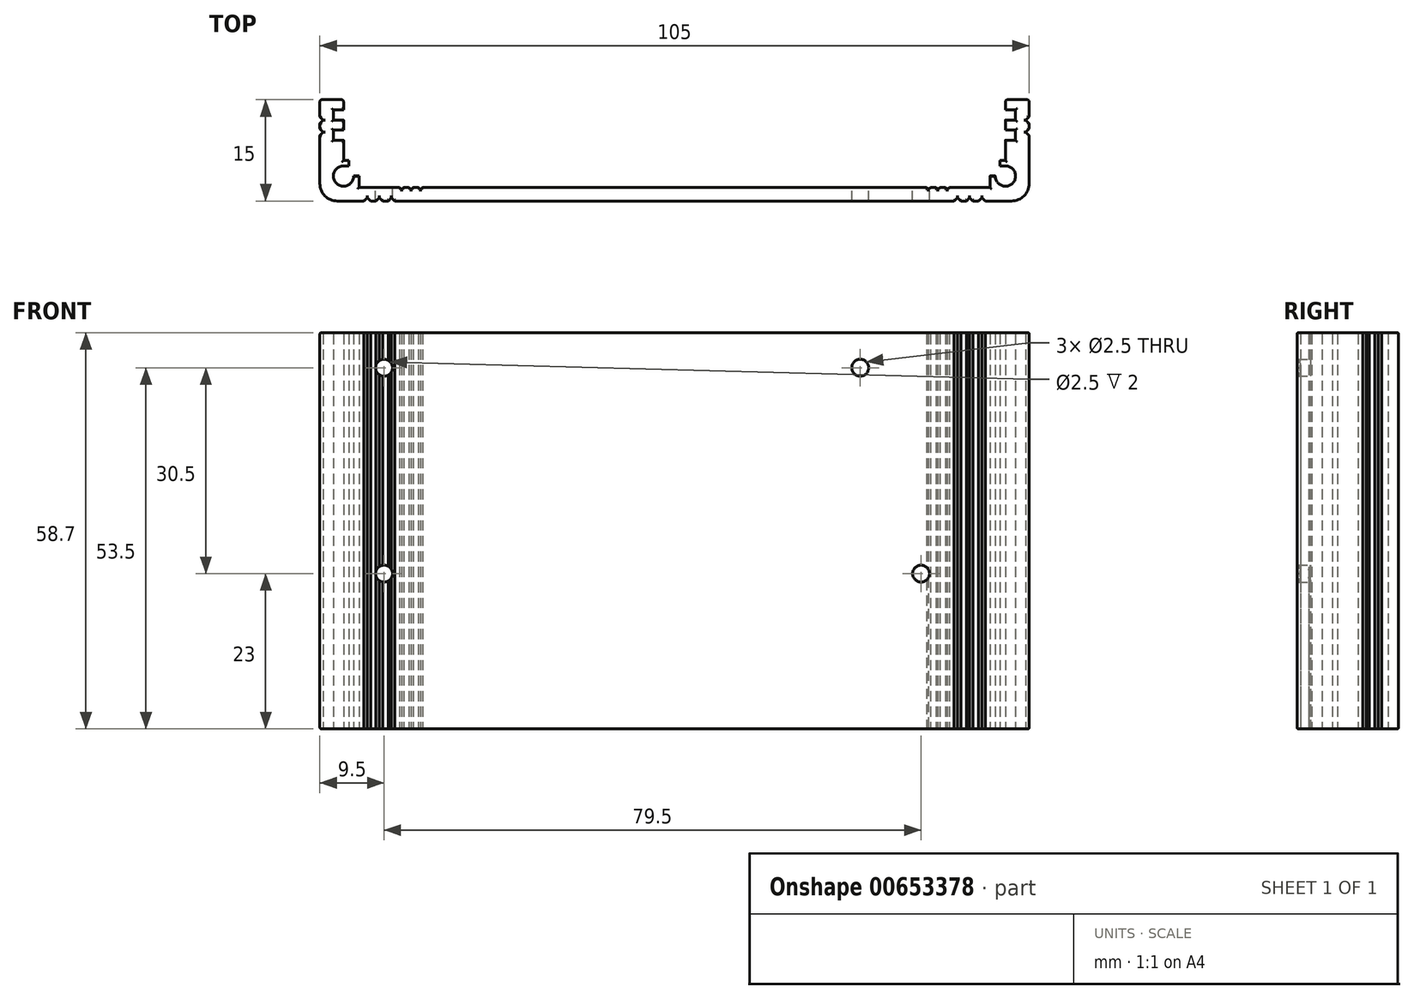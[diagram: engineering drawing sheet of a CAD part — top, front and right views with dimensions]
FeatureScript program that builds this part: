
annotation { "Feature Type Name" : "Feature", "Feature Type Description" : "" }
export const myFeature = defineFeature(function(context is Context, id is Id, definition is map)
    precondition{}
    {
        {
            var Q0;
            Q0=qCreatedBy(makeId("Top.planeOp"),FACE);
            var sketch = newSketch(context, id + "F0", { "sketchPlane" : qUnion([Q0])});
            skLineSegment(sketch, "E0.bottom", {"start": v(52.5, 15) * mm, "end": v(-52.5, 15) * mm, "construction": true});
            skLineSegment(sketch, "E0.top", {"start": v(52.5, -15) * mm, "end": v(-52.5, -15) * mm, "construction": true});
            skLineSegment(sketch, "E0.left", {"start": v(52.5, 15) * mm, "end": v(52.5, -15) * mm, "construction": true});
            skLineSegment(sketch, "E0.right", {"start": v(-52.5, 15) * mm, "end": v(-52.5, -15) * mm, "construction": true});
            skPoint(sketch, "E0.middle", {"position": v(0, 0) * mm});
            skLineSegment(sketch, "E1", {"start": v(-52.5, -15) * mm, "end": v(-46, -15) * mm});
            skLineSegment(sketch, "E2", {"start": v(-46, -15) * mm, "end": v(-45.5, -14.5) * mm});
            skLineSegment(sketch, "E3", {"start": v(-45.5, -14.5) * mm, "end": v(-45, -15) * mm});
            skLineSegment(sketch, "E4", {"start": v(-45, -15) * mm, "end": v(-44.2, -15) * mm});
            skLineSegment(sketch, "E5", {"start": v(-44.2, -15) * mm, "end": v(-43.7, -14.5) * mm});
            skLineSegment(sketch, "E6", {"start": v(-43.7, -14.5) * mm, "end": v(-43.2, -15) * mm});
            skLineSegment(sketch, "E7", {"start": v(-43.2, -15) * mm, "end": v(-42.4, -15) * mm});
            skLineSegment(sketch, "E8", {"start": v(-42.4, -15) * mm, "end": v(-41.9, -14.5) * mm});
            skLineSegment(sketch, "E9", {"start": v(-41.9, -14.5) * mm, "end": v(-41.4, -15) * mm});
            skLineSegment(sketch, "E10", {"start": v(-41.4, -15) * mm, "end": v(0, -15) * mm});
            skLineSegment(sketch, "E11.MirrorCS", {"start": v(52.5, -15) * mm, "end": v(46, -15) * mm});
            skLineSegment(sketch, "E12.MirrorCS", {"start": v(46, -15) * mm, "end": v(45.5, -14.5) * mm});
            skLineSegment(sketch, "E13.MirrorCS", {"start": v(45.5, -14.5) * mm, "end": v(45, -15) * mm});
            skLineSegment(sketch, "E14.MirrorCS", {"start": v(45, -15) * mm, "end": v(44.2, -15) * mm});
            skLineSegment(sketch, "E15.MirrorCS", {"start": v(44.2, -15) * mm, "end": v(43.7, -14.5) * mm});
            skLineSegment(sketch, "E16.MirrorCS", {"start": v(43.7, -14.5) * mm, "end": v(43.2, -15) * mm});
            skLineSegment(sketch, "E17.MirrorCS", {"start": v(43.2, -15) * mm, "end": v(42.4, -15) * mm});
            skLineSegment(sketch, "E18.MirrorCS", {"start": v(42.4, -15) * mm, "end": v(41.9, -14.5) * mm});
            skLineSegment(sketch, "E19.MirrorCS", {"start": v(41.9, -14.5) * mm, "end": v(41.4, -15) * mm});
            skLineSegment(sketch, "E20.MirrorCS", {"start": v(41.4, -15) * mm, "end": v(0, -15) * mm});
            skLineSegment(sketch, "E21", {"start": v(-52.5, 0) * mm, "end": v(-52.5, -2.5) * mm});
            skLineSegment(sketch, "E22", {"start": v(-52.5, -2.5) * mm, "end": v(-52, -3) * mm});
            skLineSegment(sketch, "E23", {"start": v(-52, -3) * mm, "end": v(-52.5, -3.5) * mm});
            skLineSegment(sketch, "E24", {"start": v(-52.5, -3.5) * mm, "end": v(-52.5, -4.3) * mm});
            skLineSegment(sketch, "E25", {"start": v(-52.5, -4.3) * mm, "end": v(-52, -4.8) * mm});
            skLineSegment(sketch, "E26", {"start": v(-52, -4.8) * mm, "end": v(-52.5, -5.3) * mm});
            skLineSegment(sketch, "E27", {"start": v(-52.5, -5.3) * mm, "end": v(-52.5, -15) * mm});
            skLineSegment(sketch, "E28.MirrorCS", {"start": v(52.5, 0) * mm, "end": v(52.5, -2.5) * mm});
            skLineSegment(sketch, "E29.MirrorCS", {"start": v(52.5, -2.5) * mm, "end": v(52, -3) * mm});
            skLineSegment(sketch, "E30.MirrorCS", {"start": v(52, -3) * mm, "end": v(52.5, -3.5) * mm});
            skLineSegment(sketch, "E31.MirrorCS", {"start": v(52.5, -4.3) * mm, "end": v(52, -4.8) * mm});
            skLineSegment(sketch, "E32.MirrorCS", {"start": v(52.5, -3.5) * mm, "end": v(52.5, -4.3) * mm});
            skLineSegment(sketch, "E33.MirrorCS", {"start": v(52, -4.8) * mm, "end": v(52.5, -5.3) * mm});
            skLineSegment(sketch, "E34.MirrorCS", {"start": v(52.5, -5.3) * mm, "end": v(52.5, -15) * mm});
            skLineSegment(sketch, "E35", {"start": v(-52.5, 0) * mm, "end": v(-49, 0) * mm});
            skLineSegment(sketch, "E36", {"start": v(-49, 0) * mm, "end": v(-49, -1.5) * mm});
            skLineSegment(sketch, "E37", {"start": v(-49, -1.5) * mm, "end": v(-50.5, -1.5) * mm});
            skLineSegment(sketch, "E38", {"start": v(-50.5, -1.5) * mm, "end": v(-50.5, -3) * mm});
            skLineSegment(sketch, "E39", {"start": v(-50.5, -3) * mm, "end": v(-49, -3) * mm});
            skLineSegment(sketch, "E40", {"start": v(-49, -3) * mm, "end": v(-49, -4.5) * mm});
            skLineSegment(sketch, "E41", {"start": v(-49, -4.5) * mm, "end": v(-50.5, -4.5) * mm});
            skLineSegment(sketch, "E42", {"start": v(-50.5, -4.5) * mm, "end": v(-50.5, -6) * mm});
            skLineSegment(sketch, "E43", {"start": v(-50.5, -6) * mm, "end": v(-49, -6) * mm});
            skLineSegment(sketch, "E44", {"start": v(-49, -6) * mm, "end": v(-49, -9) * mm});
            skCircle(sketch, "E45", {"center": v(-49, -11.3) * mm, "radius": 1.5 * mm, "construction": true});
            skPoint(sketch, "E45.second.point", {"position": v(-49, -12.8) * mm});
            skPoint(sketch, "E45.third.point", {"position": v(-47.5, -11.3) * mm});
            skLineSegment(sketch, "E46", {"start": v(-49, -12.8) * mm, "end": v(-49, -9.8) * mm, "construction": true});
            skArc(sketch, "E47", {"start": v(-49, -9.8) * mm, "mid": v(-50.06, -12.36) * mm, "end": v(-47.5, -11.3) * mm});
            skLineSegment(sketch, "E48", {"start": v(-47.5, -11.3) * mm, "end": v(-47.5, -11.3) * mm});
            skLineSegment(sketch, "E49", {"start": v(-46.7, -13) * mm, "end": v(-40.7, -13) * mm});
            skLineSegment(sketch, "E50", {"start": v(-40.7, -13) * mm, "end": v(-40.4, -13.3) * mm});
            skLineSegment(sketch, "E51", {"start": v(-40.4, -13.3) * mm, "end": v(-40.1, -13) * mm});
            skLineSegment(sketch, "E52", {"start": v(-40.1, -13) * mm, "end": v(-39.3, -13) * mm});
            skLineSegment(sketch, "E53", {"start": v(-39.3, -13) * mm, "end": v(-39, -13.3) * mm});
            skLineSegment(sketch, "E54", {"start": v(-39, -13.3) * mm, "end": v(-38.7, -13) * mm});
            skLineSegment(sketch, "E55", {"start": v(-38.7, -13) * mm, "end": v(-37.9, -13) * mm});
            skLineSegment(sketch, "E56", {"start": v(-37.9, -13) * mm, "end": v(-37.6, -13.3) * mm});
            skLineSegment(sketch, "E57", {"start": v(-37.6, -13.3) * mm, "end": v(-37.3, -13) * mm});
            skLineSegment(sketch, "E58", {"start": v(-37.3, -13) * mm, "end": v(0, -13) * mm});
            skLineSegment(sketch, "E59", {"start": v(-47.5, -11.3) * mm, "end": v(-46.7, -11.3) * mm});
            skLineSegment(sketch, "E60", {"start": v(-46.7, -11.3) * mm, "end": v(-46.7, -13) * mm});
            skLineSegment(sketch, "E61.MirrorCS", {"start": v(37.3, -13) * mm, "end": v(0, -13) * mm});
            skLineSegment(sketch, "E62.MirrorCS", {"start": v(37.6, -13.3) * mm, "end": v(37.3, -13) * mm});
            skLineSegment(sketch, "E63.MirrorCS", {"start": v(37.9, -13) * mm, "end": v(37.6, -13.3) * mm});
            skLineSegment(sketch, "E64.MirrorCS", {"start": v(39, -13.3) * mm, "end": v(38.7, -13) * mm});
            skLineSegment(sketch, "E65.MirrorCS", {"start": v(39.3, -13) * mm, "end": v(39, -13.3) * mm});
            skLineSegment(sketch, "E66.MirrorCS", {"start": v(40.4, -13.3) * mm, "end": v(40.1, -13) * mm});
            skLineSegment(sketch, "E67.MirrorCS", {"start": v(40.7, -13) * mm, "end": v(40.4, -13.3) * mm});
            skLineSegment(sketch, "E68.MirrorCS", {"start": v(46.7, -13) * mm, "end": v(40.7, -13) * mm});
            skLineSegment(sketch, "E69.MirrorCS", {"start": v(46.7, -11.3) * mm, "end": v(46.7, -13) * mm});
            skLineSegment(sketch, "E70.MirrorCS", {"start": v(49, -6) * mm, "end": v(49, -9) * mm});
            skLineSegment(sketch, "E71.MirrorCS", {"start": v(50.5, -6) * mm, "end": v(49, -6) * mm});
            skLineSegment(sketch, "E72.MirrorCS", {"start": v(50.5, -4.5) * mm, "end": v(50.5, -6) * mm});
            skLineSegment(sketch, "E73.MirrorCS", {"start": v(49, -4.5) * mm, "end": v(50.5, -4.5) * mm});
            skLineSegment(sketch, "E74.MirrorCS", {"start": v(49, -3) * mm, "end": v(49, -4.5) * mm});
            skLineSegment(sketch, "E75.MirrorCS", {"start": v(50.5, -3) * mm, "end": v(49, -3) * mm});
            skLineSegment(sketch, "E76.MirrorCS", {"start": v(50.5, -1.5) * mm, "end": v(50.5, -3) * mm});
            skLineSegment(sketch, "E77.MirrorCS", {"start": v(49, -1.5) * mm, "end": v(50.5, -1.5) * mm});
            skLineSegment(sketch, "E78.MirrorCS", {"start": v(49, 0) * mm, "end": v(49, -1.5) * mm});
            skLineSegment(sketch, "E79.MirrorCS", {"start": v(52.5, 0) * mm, "end": v(49, 0) * mm});
            skLineSegment(sketch, "E80.MirrorCS", {"start": v(38.7, -13) * mm, "end": v(37.9, -13) * mm});
            skLineSegment(sketch, "E81.MirrorCS", {"start": v(40.1, -13) * mm, "end": v(39.3, -13) * mm});
            skLineSegment(sketch, "E82", {"start": v(-49, -9) * mm, "end": v(-48.2, -9) * mm});
            skLineSegment(sketch, "E83", {"start": v(-48.2, -9) * mm, "end": v(-48.2, -9.8) * mm});
            skLineSegment(sketch, "E84", {"start": v(-48.2, -9.8) * mm, "end": v(-49, -9.8) * mm});
            skLineSegment(sketch, "E85", {"start": v(-50.5, -11.3) * mm, "end": v(-47.5, -11.3) * mm, "construction": true});
            skLineSegment(sketch, "E86", {"start": v(-50.5, -11.3) * mm, "end": v(-50.5, -1.5) * mm, "construction": true});
            skArc(sketch, "E87.MirrorCS", {"start": v(49, -9.8) * mm, "mid": v(50.06, -12.36) * mm, "end": v(47.5, -11.3) * mm});
            skLineSegment(sketch, "E88.MirrorCS", {"start": v(49, -9) * mm, "end": v(48.2, -9) * mm});
            skLineSegment(sketch, "E89.MirrorCS", {"start": v(48.2, -9.8) * mm, "end": v(49, -9.8) * mm});
            skLineSegment(sketch, "E90.MirrorCS", {"start": v(48.2, -9) * mm, "end": v(48.2, -9.8) * mm});
            skLineSegment(sketch, "E91.MirrorCS", {"start": v(47.5, -11.3) * mm, "end": v(46.7, -11.3) * mm});
            skSolve(sketch);
        }
        {
            var Q0;
            Q0=makeQuery(id+"F0.imprint","IMPRINT",FACE,{"disambiguationData":[TD([[makeQuery(id+"F0.imprint","IMPRINT",EDGE,{"derivedFrom":sQuery(id+"F0.wireOp",EDGE,"E1")}),1.0]])]});
            extrude(context, id + "F1", {"entities" : qUnion([Q0]), "depth" : 58.7 * mm, "offsetDistance" : 25.4 * mm});
        }
        {
            var Q0;
            Q0=makeQuery(id+"F1.opExtrude","CAP_FACE",FACE,{"disambiguationData":[OSD([sQuery(id+"F0.wireOp",EDGE,"E1"),sQuery(id+"F0.wireOp",EDGE,"E2"),sQuery(id+"F0.wireOp",EDGE,"E3"),sQuery(id+"F0.wireOp",EDGE,"E4"),sQuery(id+"F0.wireOp",EDGE,"E5"),sQuery(id+"F0.wireOp",EDGE,"E6"),sQuery(id+"F0.wireOp",EDGE,"E7"),sQuery(id+"F0.wireOp",EDGE,"E8"),sQuery(id+"F0.wireOp",EDGE,"E9"),sQuery(id+"F0.wireOp",EDGE,"E10"),sQuery(id+"F0.wireOp",EDGE,"E11.MirrorCS"),sQuery(id+"F0.wireOp",EDGE,"E12.MirrorCS"),sQuery(id+"F0.wireOp",EDGE,"E13.MirrorCS"),sQuery(id+"F0.wireOp",EDGE,"E14.MirrorCS"),sQuery(id+"F0.wireOp",EDGE,"E15.MirrorCS"),sQuery(id+"F0.wireOp",EDGE,"E16.MirrorCS"),sQuery(id+"F0.wireOp",EDGE,"E17.MirrorCS"),sQuery(id+"F0.wireOp",EDGE,"E18.MirrorCS"),sQuery(id+"F0.wireOp",EDGE,"E19.MirrorCS"),sQuery(id+"F0.wireOp",EDGE,"E20.MirrorCS"),sQuery(id+"F0.wireOp",EDGE,"E21"),sQuery(id+"F0.wireOp",EDGE,"E22"),sQuery(id+"F0.wireOp",EDGE,"E23"),sQuery(id+"F0.wireOp",EDGE,"E24"),sQuery(id+"F0.wireOp",EDGE,"E25"),sQuery(id+"F0.wireOp",EDGE,"E26"),sQuery(id+"F0.wireOp",EDGE,"E27"),sQuery(id+"F0.wireOp",EDGE,"E28.MirrorCS"),sQuery(id+"F0.wireOp",EDGE,"E29.MirrorCS"),sQuery(id+"F0.wireOp",EDGE,"E30.MirrorCS"),sQuery(id+"F0.wireOp",EDGE,"E31.MirrorCS"),sQuery(id+"F0.wireOp",EDGE,"E32.MirrorCS"),sQuery(id+"F0.wireOp",EDGE,"E33.MirrorCS"),sQuery(id+"F0.wireOp",EDGE,"E34.MirrorCS"),sQuery(id+"F0.wireOp",EDGE,"E35"),sQuery(id+"F0.wireOp",EDGE,"E36"),sQuery(id+"F0.wireOp",EDGE,"E37"),sQuery(id+"F0.wireOp",EDGE,"E38"),sQuery(id+"F0.wireOp",EDGE,"E39"),sQuery(id+"F0.wireOp",EDGE,"E40"),sQuery(id+"F0.wireOp",EDGE,"E41"),sQuery(id+"F0.wireOp",EDGE,"E42"),sQuery(id+"F0.wireOp",EDGE,"E43"),sQuery(id+"F0.wireOp",EDGE,"E44"),sQuery(id+"F0.wireOp",EDGE,"E47"),sQuery(id+"F0.wireOp",EDGE,"E49"),sQuery(id+"F0.wireOp",EDGE,"E50"),sQuery(id+"F0.wireOp",EDGE,"E51"),sQuery(id+"F0.wireOp",EDGE,"E52"),sQuery(id+"F0.wireOp",EDGE,"E53"),sQuery(id+"F0.wireOp",EDGE,"E54"),sQuery(id+"F0.wireOp",EDGE,"E55"),sQuery(id+"F0.wireOp",EDGE,"E56"),sQuery(id+"F0.wireOp",EDGE,"E57"),sQuery(id+"F0.wireOp",EDGE,"E58"),sQuery(id+"F0.wireOp",EDGE,"E59"),sQuery(id+"F0.wireOp",EDGE,"E60"),sQuery(id+"F0.wireOp",EDGE,"E61.MirrorCS"),sQuery(id+"F0.wireOp",EDGE,"E62.MirrorCS"),sQuery(id+"F0.wireOp",EDGE,"E63.MirrorCS"),sQuery(id+"F0.wireOp",EDGE,"E64.MirrorCS"),sQuery(id+"F0.wireOp",EDGE,"E65.MirrorCS"),sQuery(id+"F0.wireOp",EDGE,"E66.MirrorCS"),sQuery(id+"F0.wireOp",EDGE,"E67.MirrorCS"),sQuery(id+"F0.wireOp",EDGE,"E68.MirrorCS"),sQuery(id+"F0.wireOp",EDGE,"E69.MirrorCS"),sQuery(id+"F0.wireOp",EDGE,"E70.MirrorCS"),sQuery(id+"F0.wireOp",EDGE,"E71.MirrorCS"),sQuery(id+"F0.wireOp",EDGE,"E72.MirrorCS"),sQuery(id+"F0.wireOp",EDGE,"E73.MirrorCS"),sQuery(id+"F0.wireOp",EDGE,"E74.MirrorCS"),sQuery(id+"F0.wireOp",EDGE,"E75.MirrorCS"),sQuery(id+"F0.wireOp",EDGE,"E76.MirrorCS"),sQuery(id+"F0.wireOp",EDGE,"E77.MirrorCS"),sQuery(id+"F0.wireOp",EDGE,"E78.MirrorCS"),sQuery(id+"F0.wireOp",EDGE,"E79.MirrorCS"),sQuery(id+"F0.wireOp",EDGE,"E80.MirrorCS"),sQuery(id+"F0.wireOp",EDGE,"E81.MirrorCS"),sQuery(id+"F0.wireOp",EDGE,"E82"),sQuery(id+"F0.wireOp",EDGE,"E83"),sQuery(id+"F0.wireOp",EDGE,"E84"),sQuery(id+"F0.wireOp",EDGE,"E87.MirrorCS"),sQuery(id+"F0.wireOp",EDGE,"E88.MirrorCS"),sQuery(id+"F0.wireOp",EDGE,"E89.MirrorCS"),sQuery(id+"F0.wireOp",EDGE,"E90.MirrorCS"),sQuery(id+"F0.wireOp",EDGE,"E91.MirrorCS")])],"isStart":false});
            fillet(context, id + "F2", {"entities" : qUnion([Q0]), "radius" : 0.2 * mm, "tangentPropagation" : true, "allowEdgeOverflow" : false});
        }
        {
            var Q0;
            Q0=makeQuery(id+"F1.opExtrude","CAP_FACE",FACE,{"disambiguationData":[OSD([sQuery(id+"F0.wireOp",EDGE,"E1"),sQuery(id+"F0.wireOp",EDGE,"E2"),sQuery(id+"F0.wireOp",EDGE,"E3"),sQuery(id+"F0.wireOp",EDGE,"E4"),sQuery(id+"F0.wireOp",EDGE,"E5"),sQuery(id+"F0.wireOp",EDGE,"E6"),sQuery(id+"F0.wireOp",EDGE,"E7"),sQuery(id+"F0.wireOp",EDGE,"E8"),sQuery(id+"F0.wireOp",EDGE,"E9"),sQuery(id+"F0.wireOp",EDGE,"E10"),sQuery(id+"F0.wireOp",EDGE,"E11.MirrorCS"),sQuery(id+"F0.wireOp",EDGE,"E12.MirrorCS"),sQuery(id+"F0.wireOp",EDGE,"E13.MirrorCS"),sQuery(id+"F0.wireOp",EDGE,"E14.MirrorCS"),sQuery(id+"F0.wireOp",EDGE,"E15.MirrorCS"),sQuery(id+"F0.wireOp",EDGE,"E16.MirrorCS"),sQuery(id+"F0.wireOp",EDGE,"E17.MirrorCS"),sQuery(id+"F0.wireOp",EDGE,"E18.MirrorCS"),sQuery(id+"F0.wireOp",EDGE,"E19.MirrorCS"),sQuery(id+"F0.wireOp",EDGE,"E20.MirrorCS"),sQuery(id+"F0.wireOp",EDGE,"E21"),sQuery(id+"F0.wireOp",EDGE,"E22"),sQuery(id+"F0.wireOp",EDGE,"E23"),sQuery(id+"F0.wireOp",EDGE,"E24"),sQuery(id+"F0.wireOp",EDGE,"E25"),sQuery(id+"F0.wireOp",EDGE,"E26"),sQuery(id+"F0.wireOp",EDGE,"E27"),sQuery(id+"F0.wireOp",EDGE,"E28.MirrorCS"),sQuery(id+"F0.wireOp",EDGE,"E29.MirrorCS"),sQuery(id+"F0.wireOp",EDGE,"E30.MirrorCS"),sQuery(id+"F0.wireOp",EDGE,"E31.MirrorCS"),sQuery(id+"F0.wireOp",EDGE,"E32.MirrorCS"),sQuery(id+"F0.wireOp",EDGE,"E33.MirrorCS"),sQuery(id+"F0.wireOp",EDGE,"E34.MirrorCS"),sQuery(id+"F0.wireOp",EDGE,"E35"),sQuery(id+"F0.wireOp",EDGE,"E36"),sQuery(id+"F0.wireOp",EDGE,"E37"),sQuery(id+"F0.wireOp",EDGE,"E38"),sQuery(id+"F0.wireOp",EDGE,"E39"),sQuery(id+"F0.wireOp",EDGE,"E40"),sQuery(id+"F0.wireOp",EDGE,"E41"),sQuery(id+"F0.wireOp",EDGE,"E42"),sQuery(id+"F0.wireOp",EDGE,"E43"),sQuery(id+"F0.wireOp",EDGE,"E44"),sQuery(id+"F0.wireOp",EDGE,"E47"),sQuery(id+"F0.wireOp",EDGE,"E49"),sQuery(id+"F0.wireOp",EDGE,"E50"),sQuery(id+"F0.wireOp",EDGE,"E51"),sQuery(id+"F0.wireOp",EDGE,"E52"),sQuery(id+"F0.wireOp",EDGE,"E53"),sQuery(id+"F0.wireOp",EDGE,"E54"),sQuery(id+"F0.wireOp",EDGE,"E55"),sQuery(id+"F0.wireOp",EDGE,"E56"),sQuery(id+"F0.wireOp",EDGE,"E57"),sQuery(id+"F0.wireOp",EDGE,"E58"),sQuery(id+"F0.wireOp",EDGE,"E59"),sQuery(id+"F0.wireOp",EDGE,"E60"),sQuery(id+"F0.wireOp",EDGE,"E61.MirrorCS"),sQuery(id+"F0.wireOp",EDGE,"E62.MirrorCS"),sQuery(id+"F0.wireOp",EDGE,"E63.MirrorCS"),sQuery(id+"F0.wireOp",EDGE,"E64.MirrorCS"),sQuery(id+"F0.wireOp",EDGE,"E65.MirrorCS"),sQuery(id+"F0.wireOp",EDGE,"E66.MirrorCS"),sQuery(id+"F0.wireOp",EDGE,"E67.MirrorCS"),sQuery(id+"F0.wireOp",EDGE,"E68.MirrorCS"),sQuery(id+"F0.wireOp",EDGE,"E69.MirrorCS"),sQuery(id+"F0.wireOp",EDGE,"E70.MirrorCS"),sQuery(id+"F0.wireOp",EDGE,"E71.MirrorCS"),sQuery(id+"F0.wireOp",EDGE,"E72.MirrorCS"),sQuery(id+"F0.wireOp",EDGE,"E73.MirrorCS"),sQuery(id+"F0.wireOp",EDGE,"E74.MirrorCS"),sQuery(id+"F0.wireOp",EDGE,"E75.MirrorCS"),sQuery(id+"F0.wireOp",EDGE,"E76.MirrorCS"),sQuery(id+"F0.wireOp",EDGE,"E77.MirrorCS"),sQuery(id+"F0.wireOp",EDGE,"E78.MirrorCS"),sQuery(id+"F0.wireOp",EDGE,"E79.MirrorCS"),sQuery(id+"F0.wireOp",EDGE,"E80.MirrorCS"),sQuery(id+"F0.wireOp",EDGE,"E81.MirrorCS"),sQuery(id+"F0.wireOp",EDGE,"E82"),sQuery(id+"F0.wireOp",EDGE,"E83"),sQuery(id+"F0.wireOp",EDGE,"E84"),sQuery(id+"F0.wireOp",EDGE,"E87.MirrorCS"),sQuery(id+"F0.wireOp",EDGE,"E88.MirrorCS"),sQuery(id+"F0.wireOp",EDGE,"E89.MirrorCS"),sQuery(id+"F0.wireOp",EDGE,"E90.MirrorCS"),sQuery(id+"F0.wireOp",EDGE,"E91.MirrorCS")])],"isStart":true});
            fillet(context, id + "F3", {"entities" : qUnion([Q0]), "radius" : 0.2 * mm, "tangentPropagation" : true, "allowEdgeOverflow" : false});
        }
        {
            var Q0;
            Q0=makeQuery(id+"F1.opExtrude","SWEPT_EDGE",EDGE,{"disambiguationData":[OSD([sQuery(id+"F0.wireOp",EDGE,"E21"),sQuery(id+"F0.wireOp",EDGE,"E35")])]});
            var Q1;
            Q1=makeQuery(id+"F1.opExtrude","SWEPT_EDGE",EDGE,{"disambiguationData":[OSD([sQuery(id+"F0.wireOp",EDGE,"E35"),sQuery(id+"F0.wireOp",EDGE,"E36")])]});
            var Q2;
            Q2=makeQuery(id+"F1.opExtrude","SWEPT_EDGE",EDGE,{"disambiguationData":[OSD([sQuery(id+"F0.wireOp",EDGE,"E78.MirrorCS"),sQuery(id+"F0.wireOp",EDGE,"E79.MirrorCS")])]});
            var Q3;
            Q3=makeQuery(id+"F1.opExtrude","SWEPT_EDGE",EDGE,{"disambiguationData":[OSD([sQuery(id+"F0.wireOp",EDGE,"E28.MirrorCS"),sQuery(id+"F0.wireOp",EDGE,"E79.MirrorCS")])]});
            fillet(context, id + "F4", {"entities" : qUnion([Q0, Q1, Q2, Q3]), "radius" : 0.3 * mm, "tangentPropagation" : true, "allowEdgeOverflow" : false});
        }
        {
            var Q0;
            Q0=makeQuery(id+"F1.opExtrude","SWEPT_EDGE",EDGE,{"disambiguationData":[OSD([sQuery(id+"F0.wireOp",EDGE,"E1"),sQuery(id+"F0.wireOp",EDGE,"E27")])]});
            var Q1;
            Q1=makeQuery(id+"F1.opExtrude","SWEPT_EDGE",EDGE,{"disambiguationData":[OSD([sQuery(id+"F0.wireOp",EDGE,"E11.MirrorCS"),sQuery(id+"F0.wireOp",EDGE,"E34.MirrorCS")])]});
            fillet(context, id + "F5", {"entities" : qUnion([Q0, Q1]), "radius" : 2.6 * mm, "tangentPropagation" : true, "allowEdgeOverflow" : false});
        }
        {
            var Q0;
            Q0=makeQuery(id+"F1.opExtrude","SWEPT_FACE",FACE,{"disambiguationData":[OSD([sQuery(id+"F0.wireOp",EDGE,"E58"),sQuery(id+"F0.wireOp",EDGE,"E61.MirrorCS")])]});
            var sketch = newSketch(context, id + "F6", { "sketchPlane" : qUnion([Q0])});
            skLineSegment(sketch, "E92", {"start": v(0, 0.2) * mm, "end": v(0, 57.5) * mm, "construction": true});
            skLineSegment(sketch, "E93.bottom", {"start": v(47.5, 57.5) * mm, "end": v(-47.5, 57.5) * mm, "construction": true});
            skLineSegment(sketch, "E93.top", {"start": v(47.5, 19) * mm, "end": v(-47.5, 19) * mm, "construction": true});
            skLineSegment(sketch, "E93.left", {"start": v(47.5, 57.5) * mm, "end": v(47.5, 19) * mm, "construction": true});
            skLineSegment(sketch, "E93.right", {"start": v(-47.5, 57.5) * mm, "end": v(-47.5, 19) * mm, "construction": true});
            skCircle(sketch, "E94", {"center": v(-27.5, 53.5) * mm, "radius": 1.25 * mm});
            skCircle(sketch, "E95", {"center": v(-36.5, 23) * mm, "radius": 1.25 * mm});
            skCircle(sketch, "E96", {"center": v(43, 53.5) * mm, "radius": 1.25 * mm});
            skCircle(sketch, "E97", {"center": v(43, 23) * mm, "radius": 1.25 * mm});
            skSolve(sketch);
        }
        {
            var Q0;
            Q0 = qSketchRegion(id + "F6", true);
            extrude(context, id + "F7", {"entities" : qUnion([Q0]), "operationType" : NewBodyOperationType.REMOVE, "endBound" : BoundingType.UP_TO_NEXT, "oppositeDirection" : true, "depth" : 25.4 * mm, "offsetDistance" : 25.4 * mm});
        }
    });
